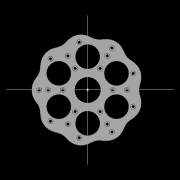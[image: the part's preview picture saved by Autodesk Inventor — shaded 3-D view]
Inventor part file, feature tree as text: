
AUTODESK INVENTOR PART (.ipt)
format: ipt  version: 2022.2 (Build 262287010, 287A)  size: 828,416 bytes
history: native  units: mm
features: other x20, extrude x17, sketch x12, pattern_circular x7, plane x4, fillet x2, move_body x2, revolve x2, draft x2, chamfer x2
ambient origin geometry x8: Origin, YZ Plane, XZ Plane, XY Plane, X Axis, Y Axis, Z Axis, Center Point
bodies: Solid5 (feature_tree)
feature tree (70):
  other  "CrossSection1"
  sketch  "Sketch7"  dims[d90=15.767323mm]
  other  "Roller1"
  other  "Roller2"
  sketch  "Sketch22"  dims[d167=8.972256mm]
  sketch  "Sketch2"  dims[d57=4.025mm]
  sketch  "Sketch23"  dims[d173=10.814812mm]
  other  "RevRoller1"
  fillet  "Fillet1"  Radius=13.336791mm
  pattern_circular  "Circular Pattern13"  Count=360  [1 undecoded]
  move_body  "Move Body7"
  revolve  "Revolution13"  [1 undecoded]
  fillet  "Fillet3"  Radius=0.025mm
  pattern_circular  "Circular Pattern14"  [2 undecoded]
  move_body  "Move Body6"
  revolve  "Revolution14"  [1 undecoded]
  other  "OuterRim_Top2"
  other  "OuterRim_Bottom2"
  extrude  "Rotor_Ring"  Depth=1.0mm
  draft  "FaceDraft2"
  sketch  "Sketch30"  dims[d201=53.5mm d232=0.0mm d233=3600.0mm]
  plane  "Work Plane5"
  other  "Rotor Featurs"
  other  "RotorRim_Bottom"
  extrude  "Extrusion24"  Depth=1.0mm
  extrude  "Extrusion25"  Depth=1.0mm
  extrude  "Extrusion26"  TaperAngle=90.0deg  [1 undecoded]
  pattern_circular  "Circular Pattern23"  [2 undecoded]
  sketch  "Sketch41"  dims[d346=0.025mm]
  extrude  "Extrusion27"  Depth=1.0mm
  extrude  "Extrusion28"  TaperAngle=360.0deg  [1 undecoded]
  pattern_circular  "Circular Pattern24"  Angle=30.0deg  [1 undecoded]
  extrude  "Extrusion29"  Depth=1.0mm
  extrude  "Extrusion30"  Depth=1.0mm
  extrude  "Extrusion31"  Depth=1.0mm
  pattern_circular  "Circular Pattern25"  [2 undecoded]
  sketch  "Sketch42"  dims[d347=0.1mm]
  extrude  "Extrusion32"  TaperAngle=30.0deg  [1 undecoded]
  extrude  "Extrusion33"  TaperAngle=90.0deg  [1 undecoded]
  extrude  "Extrusion34"  Depth=1.0mm
  extrude  "Extrusion35"  Depth=1.0mm
  pattern_circular  "Circular Pattern26"  Angle=360.0deg  [1 undecoded]
  pattern_circular  "Circular Pattern27"  Angle=90.0deg  [1 undecoded]
  chamfer  "Chamfer1"  Distance=0.1mm
  chamfer  "Chamfer2"  Distance=0.025mm
  draft  "FaceDraft4"
  plane  "Work Plane7"
  sketch  "Sketch44"  dims[d349=17.374602mm]
  sketch  "Sketch45"  dims[d350=17.374329mm]
  extrude  "Extrusion39"  Depth=1.0mm
  extrude  "Extrusion40"  Depth=1.0mm
  plane  "Work Plane8"
  sketch  "Sketch46"  dims[d351=0.025mm d352=0.025mm d354=0.025mm d355=17.374329mm d356=17.374602mm d357=1.0mm d358=90.0deg d359=0.5mm d360=60.0mm d361=360.0deg d363=30.0deg d367=8.1mm d369=4.014775mm d370=0.025mm d371=1.0mm d372=30.0deg d373=90.0deg d374=0.5mm d375=60.0mm d376=360.0deg d378=90.0deg d379=0.1mm d380=0.025mm d381=0.025mm d382=0.025mm d383=0.025mm d384=10.461905mm d385=0.0mm d386=0.0mm d391=1.0mm d392=53.5mm d393=1.5mm d394=1.5mm d395=1.5mm d396=1.5mm d397=90.0deg d398=90.0deg d399=90.0deg d400=53.5mm d401=10.461905mm d402=0.0mm d486=0.436332mm d487=0.5mm d488=2.0mm d489=0.0mm d490=20.0mm d495=2.5mm d496=8.0mm d506=13.856406mm d507=55.5mm d508=8.0mm d509=0.05mm d510=2.5mm d511=30.0deg d512=12.0mm d513=6.0mm d514=0.2mm d515=30.0deg d516=131.0mm d517=65.5mm d518=0.2mm d519=100.0mm d520=120.0mm d521=2.0mm d522=150.0mm d530=50.0mm d531=5.5mm d532=5.5mm d533=5.5mm d534=87.0mm d535=73.5mm d536=55.0mm d537=27.0mm d538=3.0mm d539=2.4mm d540=0.0mm d541=0.0mm d542=0.0mm d543=5.5mm d544=3.0mm d545=0.0mm d546=90.0mm d547=360.0deg d549=3.0mm d550=3.0mm d551=2.4mm d552=0.0mm d553=5.230953mm d554=0.0mm d555=2.4mm d556=0.0mm d557=5.230953mm d558=0.0mm d559=5.230953mm d560=0.0mm d561=90.0mm d562=360.0deg d564=60.0mm d565=360.0deg d567=5.5mm d568=5.5mm d569=3.0mm d570=0.0mm d571=5.230953mm d572=0.0mm d573=3.0mm d574=0.0mm d575=5.230953mm d576=0.0mm d577=90.0mm d578=360.0deg d580=60.0mm d581=360.0deg d584=20.0mm d585=8.0mm d587=1.75mm d589=3.0mm d592=2.0mm d593=12.0mm d594=12.0mm d600=0.5mm d601=2.0mm d602=45.0deg d603=0.5mm d604=2.0mm d605=45.0deg d606=0.436332mm d607=0.5mm d608=0.0mm d609=20.0mm d611=360.0deg d613=0.0mm d614=0.0mm d615=50.0mm d617=1.0mm d618=3.0mm d619=20.0mm d621=360.0deg d623=0.8mm d624=0.0mm d625=0.8mm d626=0.0mm d627=20.0mm d635=12.0mm d640=2.5mm d641=100.0mm d643=360.0deg d645=0.0mm d646=3600.0mm d16=0.872665mm d17=0.872665mm d49=0.872665mm d50=0.872665mm d51=0.872665mm d52=0.872665mm d236=0.5mm d237=0.872665mm d238=0.5mm d239=0.872665mm d282=1.0mm d283=1.0mm d284=1.0mm d285=0.15mm d286=0.25mm d287=0.375mm d288=14.3117mm d289=0.75mm d290=20.594885mm d291=0.0625mm d292=0.75mm d293=0.375mm d405=0.5mm d406=0.872665mm d407=0.5mm d408=0.872665mm d413=0.5mm d414=0.872665mm d415=0.5mm d416=0.872665mm d417=0.5mm d418=0.872665mm d419=0.5mm d420=0.872665mm d421=0.872665mm d431=0.5mm d432=0.872665mm d433=0.5mm d434=0.872665mm d471=0.5mm d472=0.872665mm d473=0.5mm d474=0.872665mm d497=0.5mm d498=0.872665mm d499=0.5mm d500=0.872665mm d590=0.5mm d591=0.872665mm]
  plane  "Work Plane6"
  sketch  "Sketch43"  dims[d348=0.1mm]
  extrude  "Extrusion37"  Depth=1.0mm
  extrude  "Extrusion38"  Depth=1.0mm
  other  "2D Equation Curve1"
  sketch  "Sketch40"  dims[d343=17.374329mm d344=17.374602mm d345=0.025mm]
  other  "Work Axis6"
  other  "Work Axis7"
  other  "Work Axis8"
  other  "Work Axis9"
  other  "Work Axis10"
  other  "Work Point1"
  other  "Work Point2"
  other  "Work Point3"
  other  "Work Point4"
  other  "Work Point5"
  other  "2D Equation Curve2"
note: 16 required parameter values undecoded (feature->parameter linkage not recoverable at this tier; creation-order binding heuristic only, values carry confidence <= 0.55)